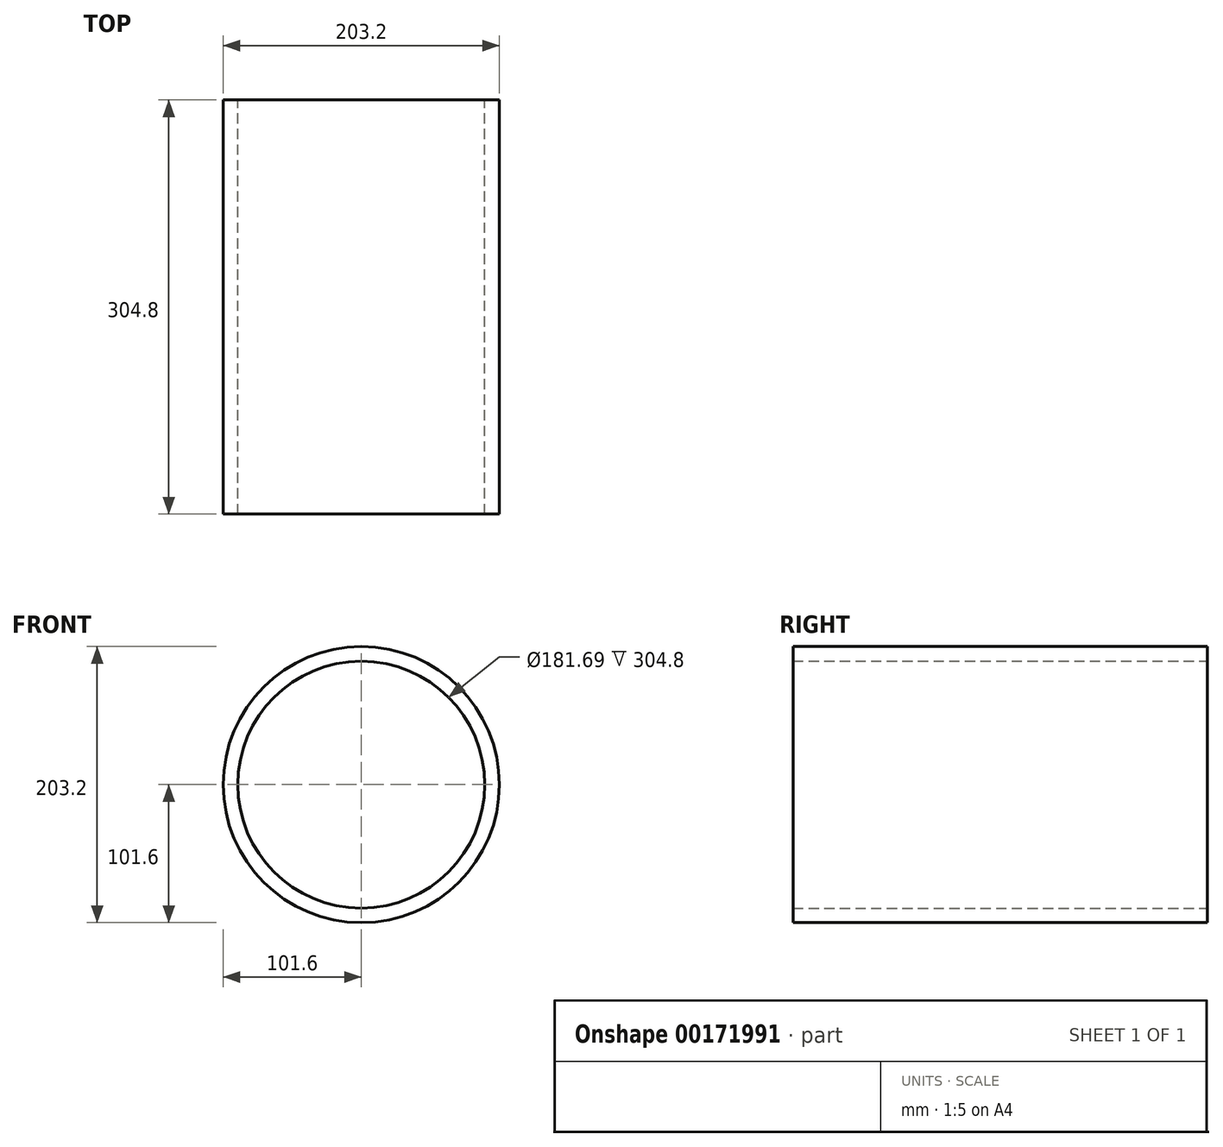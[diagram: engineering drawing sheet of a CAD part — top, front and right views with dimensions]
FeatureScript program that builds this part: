
annotation { "Feature Type Name" : "Feature", "Feature Type Description" : "" }
export const myFeature = defineFeature(function(context is Context, id is Id, definition is map)
    precondition{}
    {
        {
            var Q0;
            Q0=qCreatedBy(makeId("Front.planeOp"),FACE);
            var sketch = newSketch(context, id + "F0", { "sketchPlane" : qUnion([Q0])});
            skCircle(sketch, "E0", {"center": v(0, 0) * mm, "radius": 101.6 * mm});
            skCircle(sketch, "E1", {"center": v(0, 0) * mm, "radius": 90.85 * mm});
            skSolve(sketch);
        }
        {
            var Q0;
            Q0=qSketchRegion(id+"F0",true);
            extrude(context, id + "F1", {"entities" : qUnion([Q0]), "depth" : 304.8 * mm});
        }
    });
